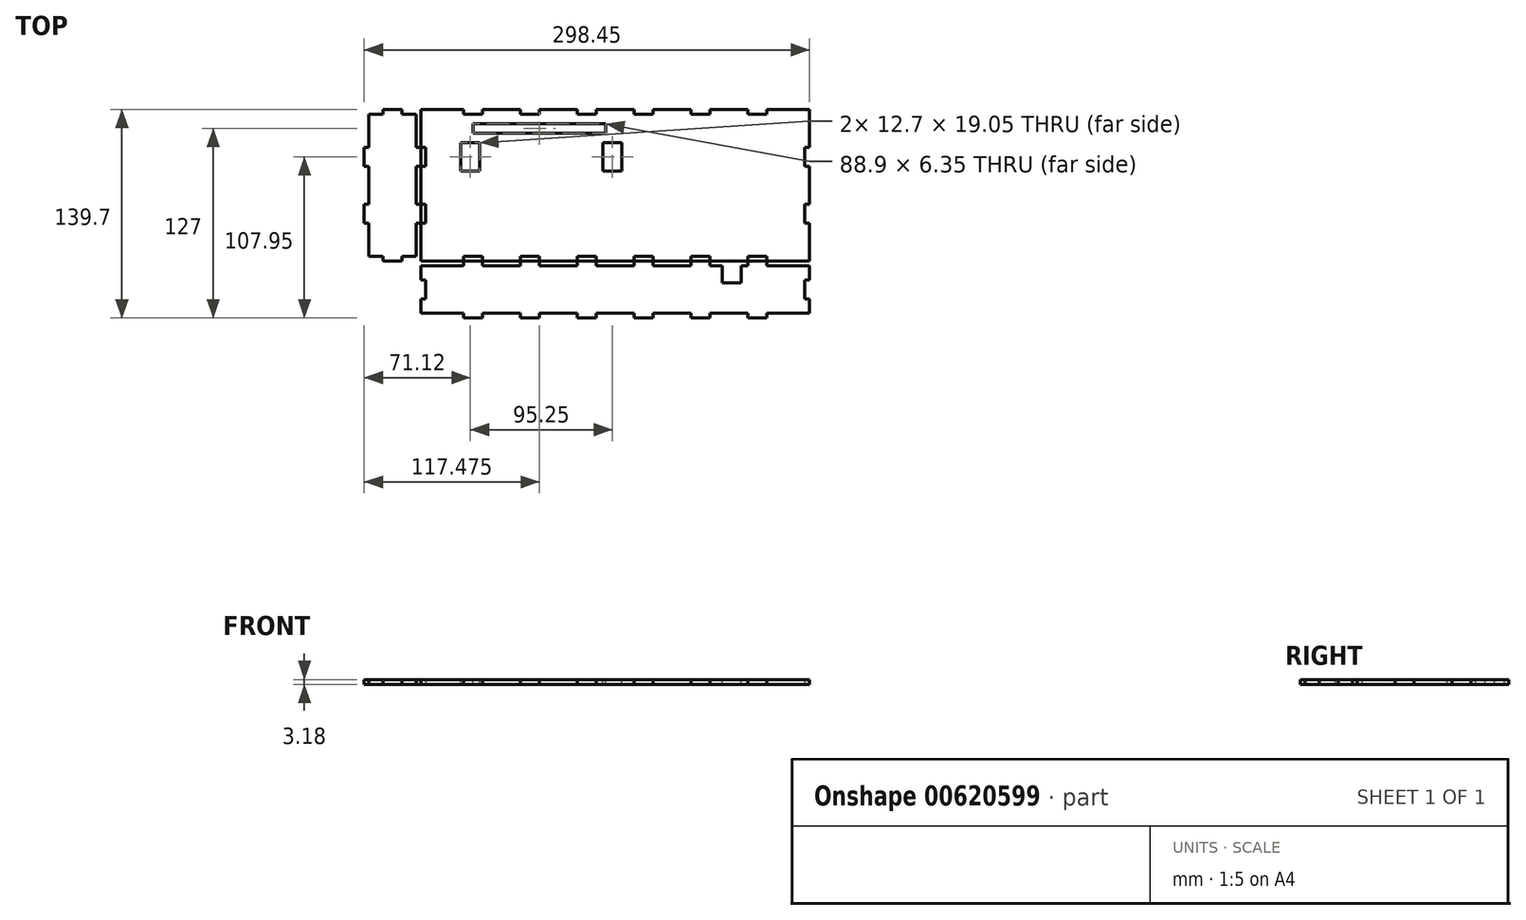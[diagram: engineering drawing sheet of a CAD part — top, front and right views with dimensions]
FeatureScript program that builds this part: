
annotation { "Feature Type Name" : "Feature", "Feature Type Description" : "" }
export const myFeature = defineFeature(function(context is Context, id is Id, definition is map)
    precondition{}
    {
        {
            var Q0;
            Q0=qCreatedBy(makeId("Top.planeOp"),FACE);
            var sketch = newSketch(context, id + "F0", { "sketchPlane" : qUnion([Q0])});
            skLineSegment(sketch, "E0.bottom", {"start": v(0, 0) * mm, "end": v(66.68, 0) * mm});
            skLineSegment(sketch, "E0.top", {"start": v(0, 101.6) * mm, "end": v(28.57, 101.6) * mm});
            skLineSegment(sketch, "E0.left", {"start": v(0, 0) * mm, "end": v(0, 25.4) * mm});
            skLineSegment(sketch, "E0.right", {"start": v(260.35, 0) * mm, "end": v(260.35, 25.4) * mm});
            skLineSegment(sketch, "E1.top", {"start": v(28.57, 98.42) * mm, "end": v(41.27, 98.42) * mm});
            skLineSegment(sketch, "E1.left", {"start": v(28.57, 101.6) * mm, "end": v(28.57, 98.42) * mm});
            skLineSegment(sketch, "E1.right", {"start": v(41.27, 101.6) * mm, "end": v(41.27, 98.42) * mm});
            skLineSegment(sketch, "E2.1.0.0", {"start": v(66.67, 98.42) * mm, "end": v(79.37, 98.42) * mm});
            skLineSegment(sketch, "E2.1.0.1", {"start": v(66.67, 101.6) * mm, "end": v(66.67, 98.42) * mm});
            skLineSegment(sketch, "E2.1.0.2", {"start": v(79.37, 101.6) * mm, "end": v(79.37, 98.42) * mm});
            skLineSegment(sketch, "E2.2.0.0", {"start": v(104.77, 98.42) * mm, "end": v(117.47, 98.42) * mm});
            skLineSegment(sketch, "E2.2.0.1", {"start": v(104.77, 101.6) * mm, "end": v(104.77, 98.42) * mm});
            skLineSegment(sketch, "E2.2.0.2", {"start": v(117.47, 101.6) * mm, "end": v(117.47, 98.42) * mm});
            skLineSegment(sketch, "E2.3.0.0", {"start": v(142.88, 98.42) * mm, "end": v(155.57, 98.42) * mm});
            skLineSegment(sketch, "E2.3.0.1", {"start": v(142.88, 101.6) * mm, "end": v(142.88, 98.42) * mm});
            skLineSegment(sketch, "E2.3.0.2", {"start": v(155.57, 101.6) * mm, "end": v(155.57, 98.42) * mm});
            skLineSegment(sketch, "E2.4.0.0", {"start": v(180.97, 98.42) * mm, "end": v(193.67, 98.42) * mm});
            skLineSegment(sketch, "E2.4.0.1", {"start": v(180.97, 101.6) * mm, "end": v(180.97, 98.42) * mm});
            skLineSegment(sketch, "E2.4.0.2", {"start": v(193.67, 101.6) * mm, "end": v(193.67, 98.42) * mm});
            skLineSegment(sketch, "E2.5.0.0", {"start": v(219.07, 98.42) * mm, "end": v(231.77, 98.42) * mm});
            skLineSegment(sketch, "E2.5.0.1", {"start": v(219.07, 101.6) * mm, "end": v(219.07, 98.42) * mm});
            skLineSegment(sketch, "E2.5.0.2", {"start": v(231.77, 101.6) * mm, "end": v(231.77, 98.42) * mm});
            skLineSegment(sketch, "E2.direction1", {"start": v(28.57, 98.42) * mm, "end": v(66.67, 98.42) * mm, "construction": true});
            skLineSegment(sketch, "E3.top", {"start": v(28.58, 3.17) * mm, "end": v(41.28, 3.17) * mm});
            skLineSegment(sketch, "E3.left", {"start": v(28.58, 0) * mm, "end": v(28.58, 3.17) * mm});
            skLineSegment(sketch, "E3.right", {"start": v(41.28, 0) * mm, "end": v(41.28, 3.17) * mm});
            skLineSegment(sketch, "E4.1.0.0", {"start": v(66.68, 3.17) * mm, "end": v(79.38, 3.17) * mm});
            skLineSegment(sketch, "E4.1.0.1", {"start": v(66.68, 0) * mm, "end": v(66.68, 3.17) * mm});
            skLineSegment(sketch, "E4.1.0.2", {"start": v(79.38, 0) * mm, "end": v(79.38, 3.17) * mm});
            skLineSegment(sketch, "E4.2.0.0", {"start": v(104.78, 3.17) * mm, "end": v(117.48, 3.17) * mm});
            skLineSegment(sketch, "E4.2.0.1", {"start": v(104.78, 0) * mm, "end": v(104.78, 3.17) * mm});
            skLineSegment(sketch, "E4.2.0.2", {"start": v(117.48, 0) * mm, "end": v(117.48, 3.17) * mm});
            skLineSegment(sketch, "E4.3.0.0", {"start": v(142.88, 3.17) * mm, "end": v(155.58, 3.17) * mm});
            skLineSegment(sketch, "E4.3.0.1", {"start": v(142.88, 0) * mm, "end": v(142.88, 3.17) * mm});
            skLineSegment(sketch, "E4.3.0.2", {"start": v(155.58, 0) * mm, "end": v(155.58, 3.17) * mm});
            skLineSegment(sketch, "E4.4.0.0", {"start": v(180.98, 3.17) * mm, "end": v(193.68, 3.17) * mm});
            skLineSegment(sketch, "E4.4.0.1", {"start": v(180.98, 0) * mm, "end": v(180.98, 3.17) * mm});
            skLineSegment(sketch, "E4.4.0.2", {"start": v(193.68, 0) * mm, "end": v(193.68, 3.17) * mm});
            skLineSegment(sketch, "E4.5.0.0", {"start": v(219.08, 3.17) * mm, "end": v(231.78, 3.17) * mm});
            skLineSegment(sketch, "E4.5.0.1", {"start": v(219.08, 0) * mm, "end": v(219.08, 3.17) * mm});
            skLineSegment(sketch, "E4.5.0.2", {"start": v(231.78, 0) * mm, "end": v(231.78, 3.17) * mm});
            skLineSegment(sketch, "E4.direction1", {"start": v(28.58, 3.17) * mm, "end": v(66.68, 3.17) * mm, "construction": true});
            skLineSegment(sketch, "E5.bottom", {"start": v(0, 76.2) * mm, "end": v(3.17, 76.2) * mm});
            skLineSegment(sketch, "E5.top", {"start": v(0, 63.5) * mm, "end": v(3.17, 63.5) * mm});
            skLineSegment(sketch, "E5.left", {"start": v(0, 76.2) * mm, "end": v(0, 63.5) * mm});
            skLineSegment(sketch, "E5.right", {"start": v(3.17, 76.2) * mm, "end": v(3.17, 63.5) * mm});
            skLineSegment(sketch, "E6.1.0.0", {"start": v(0, 38.1) * mm, "end": v(3.17, 38.1) * mm});
            skLineSegment(sketch, "E6.1.0.1", {"start": v(3.17, 38.1) * mm, "end": v(3.17, 25.4) * mm});
            skLineSegment(sketch, "E6.1.0.2", {"start": v(0, 25.4) * mm, "end": v(3.17, 25.4) * mm});
            skLineSegment(sketch, "E6.direction1", {"start": v(0, 63.5) * mm, "end": v(0, 38.1) * mm, "construction": true});
            skLineSegment(sketch, "E7.bottom", {"start": v(260.35, 76.2) * mm, "end": v(257.18, 76.2) * mm});
            skLineSegment(sketch, "E7.top", {"start": v(260.35, 63.5) * mm, "end": v(257.18, 63.5) * mm});
            skLineSegment(sketch, "E7.right", {"start": v(257.18, 76.2) * mm, "end": v(257.18, 63.5) * mm});
            skLineSegment(sketch, "E8.1.0.0", {"start": v(260.35, 38.1) * mm, "end": v(257.18, 38.1) * mm});
            skLineSegment(sketch, "E8.1.0.1", {"start": v(257.18, 38.1) * mm, "end": v(257.18, 25.4) * mm});
            skLineSegment(sketch, "E8.1.0.2", {"start": v(260.35, 25.4) * mm, "end": v(257.18, 25.4) * mm});
            skLineSegment(sketch, "E8.direction1", {"start": v(257.18, 76.2) * mm, "end": v(257.18, 38.1) * mm, "construction": true});
            skLineSegment(sketch, "E9.trimOffspring", {"start": v(41.27, 101.6) * mm, "end": v(66.67, 101.6) * mm});
            skLineSegment(sketch, "E10.trimOffspring", {"start": v(79.37, 101.6) * mm, "end": v(104.77, 101.6) * mm});
            skLineSegment(sketch, "E11.trimOffspring", {"start": v(117.47, 101.6) * mm, "end": v(142.88, 101.6) * mm});
            skLineSegment(sketch, "E12.trimOffspring", {"start": v(155.57, 101.6) * mm, "end": v(180.97, 101.6) * mm});
            skLineSegment(sketch, "E13.trimOffspring", {"start": v(193.67, 101.6) * mm, "end": v(219.07, 101.6) * mm});
            skLineSegment(sketch, "E14.trimOffspring", {"start": v(231.77, 101.6) * mm, "end": v(260.35, 101.6) * mm});
            skLineSegment(sketch, "E15.trimOffspring", {"start": v(0, 38.1) * mm, "end": v(0, 101.6) * mm});
            skLineSegment(sketch, "E16.trimOffspring", {"start": v(79.38, 0) * mm, "end": v(104.78, 0) * mm});
            skLineSegment(sketch, "E17.trimOffspring", {"start": v(117.48, 0) * mm, "end": v(142.88, 0) * mm});
            skLineSegment(sketch, "E18.trimOffspring", {"start": v(155.58, 0) * mm, "end": v(180.98, 0) * mm});
            skLineSegment(sketch, "E19.trimOffspring", {"start": v(193.68, 0) * mm, "end": v(219.08, 0) * mm});
            skLineSegment(sketch, "E20.trimOffspring", {"start": v(231.78, 0) * mm, "end": v(260.35, 0) * mm});
            skLineSegment(sketch, "E21.trimOffspring", {"start": v(260.35, 76.2) * mm, "end": v(260.35, 101.6) * mm});
            skLineSegment(sketch, "E22.trimOffspring", {"start": v(260.35, 38.1) * mm, "end": v(260.35, 63.5) * mm});
            skSolve(sketch);
        }
        {
            var Q0;
            {var subQ8=sQuery(id+"F0.wireOp",EDGE,"E0.top");Q0=makeQuery(id+"F0.imprint","IMPRINT",FACE,{"disambiguationData":[TD([[makeQuery(id+"F0.imprint","IMPRINT",EDGE,{"derivedFrom":subQ8}),-1.0]])]});}
            extrude(context, id + "F1", {"entities" : qUnion([Q0]), "depth" : 3.17 * mm, "offsetDistance" : 25.4 * mm});
        }
        {
            var Q0;
            Q0=qCreatedBy(makeId("Top.planeOp"),FACE);
            var sketch = newSketch(context, id + "F2", { "sketchPlane" : qUnion([Q0])});
            skLineSegment(sketch, "E23.bottom", {"start": v(0, 0) * mm, "end": v(41.28, 0) * mm});
            skLineSegment(sketch, "E23.top", {"start": v(28.58, -38.1) * mm, "end": v(41.28, -38.1) * mm});
            skLineSegment(sketch, "E23.left", {"start": v(0, -3.18) * mm, "end": v(0, -12.7) * mm});
            skLineSegment(sketch, "E23.right", {"start": v(260.35, -3.17) * mm, "end": v(260.35, -12.7) * mm});
            skLineSegment(sketch, "E24.top", {"start": v(0, -3.18) * mm, "end": v(28.58, -3.18) * mm});
            skLineSegment(sketch, "E24.right", {"start": v(28.58, 0) * mm, "end": v(28.58, -3.18) * mm});
            skLineSegment(sketch, "E25.top", {"start": v(41.28, -3.17) * mm, "end": v(66.68, -3.17) * mm});
            skLineSegment(sketch, "E25.left", {"start": v(41.28, 0) * mm, "end": v(41.28, -3.17) * mm});
            skLineSegment(sketch, "E25.right", {"start": v(66.68, 0) * mm, "end": v(66.68, -3.17) * mm});
            skLineSegment(sketch, "E26.1.0.0", {"start": v(79.38, 0) * mm, "end": v(79.38, -3.17) * mm});
            skLineSegment(sketch, "E26.1.0.1", {"start": v(79.38, -3.17) * mm, "end": v(104.78, -3.17) * mm});
            skLineSegment(sketch, "E26.1.0.2", {"start": v(104.78, 0) * mm, "end": v(104.78, -3.17) * mm});
            skLineSegment(sketch, "E26.2.0.0", {"start": v(117.47, 0) * mm, "end": v(117.47, -3.17) * mm});
            skLineSegment(sketch, "E26.2.0.1", {"start": v(117.47, -3.17) * mm, "end": v(142.88, -3.17) * mm});
            skLineSegment(sketch, "E26.2.0.2", {"start": v(142.88, 0) * mm, "end": v(142.88, -3.17) * mm});
            skLineSegment(sketch, "E26.3.0.0", {"start": v(155.57, 0) * mm, "end": v(155.57, -3.17) * mm});
            skLineSegment(sketch, "E26.3.0.1", {"start": v(155.57, -3.17) * mm, "end": v(180.97, -3.17) * mm});
            skLineSegment(sketch, "E26.3.0.2", {"start": v(180.97, 0) * mm, "end": v(180.97, -3.17) * mm});
            skLineSegment(sketch, "E26.4.0.0", {"start": v(193.67, 0) * mm, "end": v(193.67, -3.17) * mm});
            skLineSegment(sketch, "E26.4.0.1", {"start": v(193.67, -3.17) * mm, "end": v(219.07, -3.17) * mm});
            skLineSegment(sketch, "E26.4.0.2", {"start": v(219.07, 0) * mm, "end": v(219.07, -3.17) * mm});
            skLineSegment(sketch, "E26.direction1", {"start": v(41.28, -3.17) * mm, "end": v(79.38, -3.17) * mm, "construction": true});
            skLineSegment(sketch, "E27.top", {"start": v(231.78, -3.17) * mm, "end": v(260.35, -3.17) * mm});
            skLineSegment(sketch, "E27.left", {"start": v(231.78, 0) * mm, "end": v(231.78, -3.17) * mm});
            skLineSegment(sketch, "E28.bottom", {"start": v(0, -12.7) * mm, "end": v(3.18, -12.7) * mm});
            skLineSegment(sketch, "E28.top", {"start": v(0, -25.4) * mm, "end": v(3.18, -25.4) * mm});
            skLineSegment(sketch, "E28.right", {"start": v(3.18, -12.7) * mm, "end": v(3.18, -25.4) * mm});
            skLineSegment(sketch, "E29.top", {"start": v(0, -34.93) * mm, "end": v(28.58, -34.93) * mm});
            skLineSegment(sketch, "E29.right", {"start": v(28.58, -38.1) * mm, "end": v(28.58, -34.93) * mm});
            skLineSegment(sketch, "E30.top", {"start": v(41.28, -34.93) * mm, "end": v(66.68, -34.93) * mm});
            skLineSegment(sketch, "E30.left", {"start": v(41.28, -38.1) * mm, "end": v(41.28, -34.93) * mm});
            skLineSegment(sketch, "E30.right", {"start": v(66.68, -38.1) * mm, "end": v(66.68, -34.93) * mm});
            skLineSegment(sketch, "E31.1.0.0", {"start": v(79.38, -38.1) * mm, "end": v(79.38, -34.93) * mm});
            skLineSegment(sketch, "E31.1.0.1", {"start": v(79.38, -34.93) * mm, "end": v(104.78, -34.93) * mm});
            skLineSegment(sketch, "E31.1.0.2", {"start": v(104.78, -38.1) * mm, "end": v(104.78, -34.93) * mm});
            skLineSegment(sketch, "E31.2.0.0", {"start": v(117.47, -38.1) * mm, "end": v(117.47, -34.93) * mm});
            skLineSegment(sketch, "E31.2.0.1", {"start": v(117.47, -34.93) * mm, "end": v(142.88, -34.93) * mm});
            skLineSegment(sketch, "E31.2.0.2", {"start": v(142.88, -38.1) * mm, "end": v(142.88, -34.93) * mm});
            skLineSegment(sketch, "E31.3.0.0", {"start": v(155.57, -38.1) * mm, "end": v(155.57, -34.93) * mm});
            skLineSegment(sketch, "E31.3.0.1", {"start": v(155.57, -34.93) * mm, "end": v(180.97, -34.93) * mm});
            skLineSegment(sketch, "E31.3.0.2", {"start": v(180.97, -38.1) * mm, "end": v(180.97, -34.93) * mm});
            skLineSegment(sketch, "E31.4.0.0", {"start": v(193.67, -38.1) * mm, "end": v(193.67, -34.93) * mm});
            skLineSegment(sketch, "E31.4.0.1", {"start": v(193.67, -34.93) * mm, "end": v(219.07, -34.93) * mm});
            skLineSegment(sketch, "E31.4.0.2", {"start": v(219.07, -38.1) * mm, "end": v(219.07, -34.93) * mm});
            skLineSegment(sketch, "E31.direction1", {"start": v(66.68, -38.1) * mm, "end": v(79.38, -38.1) * mm, "construction": true});
            skLineSegment(sketch, "E32.top", {"start": v(231.78, -34.92) * mm, "end": v(260.35, -34.92) * mm});
            skLineSegment(sketch, "E32.left", {"start": v(231.78, -38.1) * mm, "end": v(231.78, -34.92) * mm});
            skLineSegment(sketch, "E33.bottom", {"start": v(260.35, -12.7) * mm, "end": v(257.18, -12.7) * mm});
            skLineSegment(sketch, "E33.top", {"start": v(260.35, -25.4) * mm, "end": v(257.18, -25.4) * mm});
            skLineSegment(sketch, "E33.right", {"start": v(257.18, -12.7) * mm, "end": v(257.18, -25.4) * mm});
            skLineSegment(sketch, "E34.trimOffspring", {"start": v(104.78, 0) * mm, "end": v(117.47, 0) * mm});
            skLineSegment(sketch, "E35.trimOffspring", {"start": v(66.68, 0) * mm, "end": v(79.38, 0) * mm});
            skLineSegment(sketch, "E36.trimOffspring", {"start": v(142.88, 0) * mm, "end": v(155.57, 0) * mm});
            skLineSegment(sketch, "E37.trimOffspring", {"start": v(180.97, 0) * mm, "end": v(193.67, 0) * mm});
            skLineSegment(sketch, "E38.trimOffspring", {"start": v(219.07, 0) * mm, "end": v(231.78, 0) * mm});
            skLineSegment(sketch, "E39.trimOffspring", {"start": v(260.35, -25.4) * mm, "end": v(260.35, -34.92) * mm});
            skLineSegment(sketch, "E40.trimOffspring", {"start": v(219.07, -38.1) * mm, "end": v(231.78, -38.1) * mm});
            skLineSegment(sketch, "E41.trimOffspring", {"start": v(180.97, -38.1) * mm, "end": v(193.67, -38.1) * mm});
            skLineSegment(sketch, "E42.trimOffspring", {"start": v(142.88, -38.1) * mm, "end": v(155.57, -38.1) * mm});
            skLineSegment(sketch, "E43.trimOffspring", {"start": v(104.78, -38.1) * mm, "end": v(117.47, -38.1) * mm});
            skLineSegment(sketch, "E44.trimOffspring", {"start": v(66.68, -38.1) * mm, "end": v(79.38, -38.1) * mm});
            skLineSegment(sketch, "E45.trimOffspring", {"start": v(0, -25.4) * mm, "end": v(0, -34.92) * mm});
            skSolve(sketch);
        }
        {
            var Q0;
            Q0=makeQuery(id+"F2.imprint","IMPRINT",FACE,{"disambiguationData":[TD([[makeQuery(id+"F2.imprint","IMPRINT",EDGE,{"derivedFrom":sQuery(id+"F2.wireOp",EDGE,"E23.top")}),1.0]])]});
            extrude(context, id + "F3", {"entities" : qUnion([Q0]), "depth" : 3.17 * mm, "offsetDistance" : 25.4 * mm});
        }
        {
            var Q0;
            Q0=qCreatedBy(makeId("Top.planeOp"),FACE);
            var sketch = newSketch(context, id + "F4", { "sketchPlane" : qUnion([Q0])});
            skLineSegment(sketch, "E46.left", {"start": v(0, 0) * mm, "end": v(0, 38.1) * mm});
            skLineSegment(sketch, "E46.right", {"start": v(-38.1, 25.4) * mm, "end": v(-38.1, 38.1) * mm});
            skLineSegment(sketch, "E47.top", {"start": v(0, 25.4) * mm, "end": v(-3.18, 25.4) * mm});
            skLineSegment(sketch, "E47.right", {"start": v(-3.17, 3.17) * mm, "end": v(-3.18, 25.4) * mm});
            skLineSegment(sketch, "E48.top", {"start": v(0, 76.2) * mm, "end": v(-3.18, 76.2) * mm});
            skLineSegment(sketch, "E48.right", {"start": v(-3.18, 98.42) * mm, "end": v(-3.18, 76.2) * mm});
            skLineSegment(sketch, "E49.bottom", {"start": v(0, 63.5) * mm, "end": v(-3.18, 63.5) * mm});
            skLineSegment(sketch, "E49.top", {"start": v(0, 38.1) * mm, "end": v(-3.18, 38.1) * mm});
            skLineSegment(sketch, "E49.right", {"start": v(-3.18, 63.5) * mm, "end": v(-3.18, 38.1) * mm});
            skLineSegment(sketch, "E50.MirrorCS", {"start": v(-34.93, 98.43) * mm, "end": v(-34.93, 76.2) * mm});
            skLineSegment(sketch, "E51.MirrorCS", {"start": v(-38.1, 76.2) * mm, "end": v(-34.93, 76.2) * mm});
            skLineSegment(sketch, "E52.MirrorCS", {"start": v(-38.1, 63.5) * mm, "end": v(-34.93, 63.5) * mm});
            skLineSegment(sketch, "E53.MirrorCS", {"start": v(-34.93, 63.5) * mm, "end": v(-34.93, 38.1) * mm});
            skLineSegment(sketch, "E54.MirrorCS", {"start": v(-38.1, 38.1) * mm, "end": v(-34.93, 38.1) * mm});
            skLineSegment(sketch, "E55.MirrorCS", {"start": v(-38.1, 25.4) * mm, "end": v(-34.93, 25.4) * mm});
            skLineSegment(sketch, "E56.MirrorCS", {"start": v(-34.93, 3.17) * mm, "end": v(-34.93, 25.4) * mm});
            skLineSegment(sketch, "E57.bottom", {"start": v(-25.4, 0) * mm, "end": v(-12.7, 0) * mm});
            skLineSegment(sketch, "E57.left", {"start": v(-25.4, 0) * mm, "end": v(-25.4, 3.17) * mm});
            skLineSegment(sketch, "E57.right", {"start": v(-12.7, 0) * mm, "end": v(-12.7, 3.18) * mm});
            skLineSegment(sketch, "E58.bottom", {"start": v(-25.4, 101.6) * mm, "end": v(-12.7, 101.6) * mm});
            skLineSegment(sketch, "E58.left", {"start": v(-25.4, 101.6) * mm, "end": v(-25.4, 98.43) * mm});
            skLineSegment(sketch, "E58.right", {"start": v(-12.7, 101.6) * mm, "end": v(-12.7, 98.43) * mm});
            skLineSegment(sketch, "E59", {"start": v(-25.4, 98.43) * mm, "end": v(-34.93, 98.43) * mm});
            skLineSegment(sketch, "E60", {"start": v(-34.93, 98.43) * mm, "end": v(-25.4, 98.43) * mm});
            skLineSegment(sketch, "E61", {"start": v(-25.4, 3.17) * mm, "end": v(-34.93, 3.17) * mm});
            skLineSegment(sketch, "E62", {"start": v(-34.93, 3.17) * mm, "end": v(-25.4, 3.17) * mm});
            skLineSegment(sketch, "E63.trimOffspring", {"start": v(-12.7, 0) * mm, "end": v(-25.4, 0) * mm});
            skLineSegment(sketch, "E64.trimOffspring", {"start": v(-12.7, 3.17) * mm, "end": v(-3.18, 3.17) * mm});
            skLineSegment(sketch, "E65.trimOffspring", {"start": v(-38.1, 63.5) * mm, "end": v(-38.1, 76.2) * mm});
            skLineSegment(sketch, "E66.trimOffspring", {"start": v(0, 63.5) * mm, "end": v(0, 76.2) * mm});
            skLineSegment(sketch, "E67.trimOffspring", {"start": v(-12.7, 101.6) * mm, "end": v(-25.4, 101.6) * mm});
            skLineSegment(sketch, "E68.trimOffspring", {"start": v(-12.7, 98.43) * mm, "end": v(-3.18, 98.42) * mm});
            skSolve(sketch);
        }
        {
            var Q0;
            Q0 = qSketchRegion(id + "F4", true);
            extrude(context, id + "F5", {"entities" : qUnion([Q0]), "depth" : 3.17 * mm, "offsetDistance" : 25.4 * mm});
        }
        {
            var Q0;
            Q0=makeQuery(id+"F1.opExtrude","CAP_FACE",FACE,{"disambiguationData":[OSD([sQuery(id+"F0.wireOp",EDGE,"E0.bottom"),sQuery(id+"F0.wireOp",EDGE,"E0.top"),sQuery(id+"F0.wireOp",EDGE,"E0.left"),sQuery(id+"F0.wireOp",EDGE,"E0.right"),sQuery(id+"F0.wireOp",EDGE,"E1.top"),sQuery(id+"F0.wireOp",EDGE,"E1.left"),sQuery(id+"F0.wireOp",EDGE,"E1.right"),sQuery(id+"F0.wireOp",EDGE,"E2.1.0.0"),sQuery(id+"F0.wireOp",EDGE,"E2.1.0.1"),sQuery(id+"F0.wireOp",EDGE,"E2.1.0.2"),sQuery(id+"F0.wireOp",EDGE,"E2.2.0.0"),sQuery(id+"F0.wireOp",EDGE,"E2.2.0.1"),sQuery(id+"F0.wireOp",EDGE,"E2.2.0.2"),sQuery(id+"F0.wireOp",EDGE,"E2.3.0.0"),sQuery(id+"F0.wireOp",EDGE,"E2.3.0.1"),sQuery(id+"F0.wireOp",EDGE,"E2.3.0.2"),sQuery(id+"F0.wireOp",EDGE,"E2.4.0.0"),sQuery(id+"F0.wireOp",EDGE,"E2.4.0.1"),sQuery(id+"F0.wireOp",EDGE,"E2.4.0.2"),sQuery(id+"F0.wireOp",EDGE,"E2.5.0.0"),sQuery(id+"F0.wireOp",EDGE,"E2.5.0.1"),sQuery(id+"F0.wireOp",EDGE,"E2.5.0.2"),sQuery(id+"F0.wireOp",EDGE,"E3.top"),sQuery(id+"F0.wireOp",EDGE,"E3.left"),sQuery(id+"F0.wireOp",EDGE,"E3.right"),sQuery(id+"F0.wireOp",EDGE,"E4.1.0.0"),sQuery(id+"F0.wireOp",EDGE,"E4.1.0.1"),sQuery(id+"F0.wireOp",EDGE,"E4.1.0.2"),sQuery(id+"F0.wireOp",EDGE,"E4.2.0.0"),sQuery(id+"F0.wireOp",EDGE,"E4.2.0.1"),sQuery(id+"F0.wireOp",EDGE,"E4.2.0.2"),sQuery(id+"F0.wireOp",EDGE,"E4.3.0.0"),sQuery(id+"F0.wireOp",EDGE,"E4.3.0.1"),sQuery(id+"F0.wireOp",EDGE,"E4.3.0.2"),sQuery(id+"F0.wireOp",EDGE,"E4.4.0.0"),sQuery(id+"F0.wireOp",EDGE,"E4.4.0.1"),sQuery(id+"F0.wireOp",EDGE,"E4.4.0.2"),sQuery(id+"F0.wireOp",EDGE,"E4.5.0.0"),sQuery(id+"F0.wireOp",EDGE,"E4.5.0.1"),sQuery(id+"F0.wireOp",EDGE,"E4.5.0.2"),sQuery(id+"F0.wireOp",EDGE,"E5.bottom"),sQuery(id+"F0.wireOp",EDGE,"E5.top"),sQuery(id+"F0.wireOp",EDGE,"E5.right"),sQuery(id+"F0.wireOp",EDGE,"E6.1.0.0"),sQuery(id+"F0.wireOp",EDGE,"E6.1.0.1"),sQuery(id+"F0.wireOp",EDGE,"E6.1.0.2"),sQuery(id+"F0.wireOp",EDGE,"E7.bottom"),sQuery(id+"F0.wireOp",EDGE,"E7.top"),sQuery(id+"F0.wireOp",EDGE,"E7.right"),sQuery(id+"F0.wireOp",EDGE,"E8.1.0.0"),sQuery(id+"F0.wireOp",EDGE,"E8.1.0.1"),sQuery(id+"F0.wireOp",EDGE,"E8.1.0.2"),sQuery(id+"F0.wireOp",EDGE,"E9.trimOffspring"),sQuery(id+"F0.wireOp",EDGE,"E10.trimOffspring"),sQuery(id+"F0.wireOp",EDGE,"E11.trimOffspring"),sQuery(id+"F0.wireOp",EDGE,"E12.trimOffspring"),sQuery(id+"F0.wireOp",EDGE,"E13.trimOffspring"),sQuery(id+"F0.wireOp",EDGE,"E14.trimOffspring"),sQuery(id+"F0.wireOp",EDGE,"E15.trimOffspring"),sQuery(id+"F0.wireOp",EDGE,"E16.trimOffspring"),sQuery(id+"F0.wireOp",EDGE,"E17.trimOffspring"),sQuery(id+"F0.wireOp",EDGE,"E18.trimOffspring"),sQuery(id+"F0.wireOp",EDGE,"E19.trimOffspring"),sQuery(id+"F0.wireOp",EDGE,"E20.trimOffspring"),sQuery(id+"F0.wireOp",EDGE,"E21.trimOffspring"),sQuery(id+"F0.wireOp",EDGE,"E22.trimOffspring")])],"isStart":false});
            var sketch = newSketch(context, id + "F6", { "sketchPlane" : qUnion([Q0])});
            skLineSegment(sketch, "E69.0.0", {"start": v(41.28, 3.17) * mm, "end": v(41.28, 0) * mm});
            skLineSegment(sketch, "E69.0.1", {"start": v(41.28, 0) * mm, "end": v(66.68, 0) * mm});
            skLineSegment(sketch, "E69.0.2", {"start": v(66.68, 0) * mm, "end": v(66.68, 3.17) * mm});
            skLineSegment(sketch, "E69.0.3", {"start": v(66.68, 3.17) * mm, "end": v(79.38, 3.17) * mm});
            skLineSegment(sketch, "E69.0.4", {"start": v(79.38, 3.17) * mm, "end": v(79.38, 0) * mm});
            skLineSegment(sketch, "E69.0.5", {"start": v(79.38, 0) * mm, "end": v(104.78, 0) * mm});
            skLineSegment(sketch, "E69.0.6", {"start": v(104.78, 0) * mm, "end": v(104.78, 3.17) * mm});
            skLineSegment(sketch, "E69.0.7", {"start": v(104.78, 3.17) * mm, "end": v(117.48, 3.17) * mm});
            skLineSegment(sketch, "E69.0.8", {"start": v(117.48, 3.17) * mm, "end": v(117.48, 0) * mm});
            skLineSegment(sketch, "E69.0.9", {"start": v(117.48, 0) * mm, "end": v(142.88, 0) * mm});
            skLineSegment(sketch, "E69.0.10", {"start": v(142.88, 0) * mm, "end": v(142.88, 3.17) * mm});
            skLineSegment(sketch, "E69.0.11", {"start": v(142.88, 3.17) * mm, "end": v(155.58, 3.17) * mm});
            skLineSegment(sketch, "E69.0.12", {"start": v(155.58, 3.17) * mm, "end": v(155.58, 0) * mm});
            skLineSegment(sketch, "E69.0.13", {"start": v(155.58, 0) * mm, "end": v(180.98, 0) * mm});
            skLineSegment(sketch, "E69.0.14", {"start": v(180.98, 0) * mm, "end": v(180.98, 3.17) * mm});
            skLineSegment(sketch, "E69.0.15", {"start": v(180.98, 3.17) * mm, "end": v(193.68, 3.17) * mm});
            skLineSegment(sketch, "E69.0.16", {"start": v(193.68, 3.17) * mm, "end": v(193.68, 0) * mm});
            skLineSegment(sketch, "E69.0.17", {"start": v(193.68, 0) * mm, "end": v(219.08, 0) * mm});
            skLineSegment(sketch, "E69.0.18", {"start": v(219.08, 0) * mm, "end": v(219.08, 3.17) * mm});
            skLineSegment(sketch, "E69.0.19", {"start": v(219.08, 3.17) * mm, "end": v(231.78, 3.17) * mm});
            skLineSegment(sketch, "E69.0.20", {"start": v(231.78, 3.17) * mm, "end": v(231.78, 0) * mm});
            skLineSegment(sketch, "E69.0.21", {"start": v(231.78, 0) * mm, "end": v(260.35, 0) * mm});
            skLineSegment(sketch, "E69.0.22", {"start": v(260.35, 0) * mm, "end": v(260.35, 25.4) * mm});
            skLineSegment(sketch, "E69.0.23", {"start": v(260.35, 25.4) * mm, "end": v(257.18, 25.4) * mm});
            skLineSegment(sketch, "E69.0.24", {"start": v(257.18, 25.4) * mm, "end": v(257.18, 38.1) * mm});
            skLineSegment(sketch, "E69.0.25", {"start": v(257.18, 38.1) * mm, "end": v(260.35, 38.1) * mm});
            skLineSegment(sketch, "E69.0.26", {"start": v(260.35, 38.1) * mm, "end": v(260.35, 63.5) * mm});
            skLineSegment(sketch, "E69.0.27", {"start": v(260.35, 63.5) * mm, "end": v(257.18, 63.5) * mm});
            skLineSegment(sketch, "E69.0.28", {"start": v(257.18, 63.5) * mm, "end": v(257.18, 76.2) * mm});
            skLineSegment(sketch, "E69.0.29", {"start": v(257.18, 76.2) * mm, "end": v(260.35, 76.2) * mm});
            skLineSegment(sketch, "E69.0.30", {"start": v(260.35, 76.2) * mm, "end": v(260.35, 101.6) * mm});
            skLineSegment(sketch, "E69.0.31", {"start": v(260.35, 101.6) * mm, "end": v(231.77, 101.6) * mm});
            skLineSegment(sketch, "E69.0.32", {"start": v(231.77, 101.6) * mm, "end": v(231.77, 98.42) * mm});
            skLineSegment(sketch, "E69.0.33", {"start": v(231.77, 98.42) * mm, "end": v(219.07, 98.42) * mm});
            skLineSegment(sketch, "E69.0.34", {"start": v(219.07, 98.42) * mm, "end": v(219.07, 101.6) * mm});
            skLineSegment(sketch, "E69.0.35", {"start": v(219.07, 101.6) * mm, "end": v(193.67, 101.6) * mm});
            skLineSegment(sketch, "E69.0.36", {"start": v(193.67, 101.6) * mm, "end": v(193.67, 98.42) * mm});
            skLineSegment(sketch, "E69.0.37", {"start": v(193.67, 98.42) * mm, "end": v(180.97, 98.42) * mm});
            skLineSegment(sketch, "E69.0.38", {"start": v(180.97, 98.42) * mm, "end": v(180.97, 101.6) * mm});
            skLineSegment(sketch, "E69.0.39", {"start": v(180.97, 101.6) * mm, "end": v(155.57, 101.6) * mm});
            skLineSegment(sketch, "E69.0.40", {"start": v(155.57, 101.6) * mm, "end": v(155.57, 98.42) * mm});
            skLineSegment(sketch, "E69.0.41", {"start": v(155.57, 98.42) * mm, "end": v(142.88, 98.42) * mm});
            skLineSegment(sketch, "E69.0.42", {"start": v(142.88, 98.42) * mm, "end": v(142.88, 101.6) * mm});
            skLineSegment(sketch, "E69.0.43", {"start": v(142.88, 101.6) * mm, "end": v(117.47, 101.6) * mm});
            skLineSegment(sketch, "E69.0.44", {"start": v(117.47, 101.6) * mm, "end": v(117.47, 98.42) * mm});
            skLineSegment(sketch, "E69.0.45", {"start": v(117.47, 98.42) * mm, "end": v(104.77, 98.42) * mm});
            skLineSegment(sketch, "E69.0.46", {"start": v(104.77, 98.42) * mm, "end": v(104.77, 101.6) * mm});
            skLineSegment(sketch, "E69.0.47", {"start": v(104.77, 101.6) * mm, "end": v(79.37, 101.6) * mm});
            skLineSegment(sketch, "E69.0.48", {"start": v(79.37, 101.6) * mm, "end": v(79.37, 98.42) * mm});
            skLineSegment(sketch, "E69.0.49", {"start": v(79.37, 98.42) * mm, "end": v(66.67, 98.42) * mm});
            skLineSegment(sketch, "E69.0.50", {"start": v(66.67, 98.42) * mm, "end": v(66.67, 101.6) * mm});
            skLineSegment(sketch, "E69.0.51", {"start": v(66.67, 101.6) * mm, "end": v(41.27, 101.6) * mm});
            skLineSegment(sketch, "E69.0.52", {"start": v(41.27, 101.6) * mm, "end": v(41.27, 98.42) * mm});
            skLineSegment(sketch, "E69.0.53", {"start": v(41.27, 98.42) * mm, "end": v(28.57, 98.42) * mm});
            skLineSegment(sketch, "E69.0.54", {"start": v(28.57, 98.42) * mm, "end": v(28.57, 101.6) * mm});
            skLineSegment(sketch, "E69.0.55", {"start": v(28.57, 101.6) * mm, "end": v(0, 101.6) * mm});
            skLineSegment(sketch, "E69.0.56", {"start": v(0, 101.6) * mm, "end": v(0, 76.2) * mm});
            skLineSegment(sketch, "E69.0.57", {"start": v(0, 76.2) * mm, "end": v(3.17, 76.2) * mm});
            skLineSegment(sketch, "E69.0.58", {"start": v(3.17, 76.2) * mm, "end": v(3.17, 63.5) * mm});
            skLineSegment(sketch, "E69.0.59", {"start": v(3.17, 63.5) * mm, "end": v(0, 63.5) * mm});
            skLineSegment(sketch, "E69.0.60", {"start": v(0, 63.5) * mm, "end": v(0, 38.1) * mm});
            skLineSegment(sketch, "E69.0.61", {"start": v(0, 38.1) * mm, "end": v(3.17, 38.1) * mm});
            skLineSegment(sketch, "E69.0.62", {"start": v(3.17, 38.1) * mm, "end": v(3.17, 25.4) * mm});
            skLineSegment(sketch, "E69.0.63", {"start": v(3.17, 25.4) * mm, "end": v(0, 25.4) * mm});
            skLineSegment(sketch, "E69.0.64", {"start": v(0, 25.4) * mm, "end": v(0, 0) * mm});
            skLineSegment(sketch, "E69.0.65", {"start": v(0, 0) * mm, "end": v(28.58, 0) * mm});
            skLineSegment(sketch, "E69.0.66", {"start": v(28.58, 0) * mm, "end": v(28.58, 3.17) * mm});
            skLineSegment(sketch, "E69.0.67", {"start": v(28.58, 3.17) * mm, "end": v(41.28, 3.17) * mm});
            skLineSegment(sketch, "E70.bottom", {"start": v(34.92, 92.07) * mm, "end": v(123.82, 92.07) * mm});
            skLineSegment(sketch, "E70.top", {"start": v(34.92, 85.72) * mm, "end": v(123.82, 85.72) * mm});
            skLineSegment(sketch, "E70.left", {"start": v(34.92, 92.07) * mm, "end": v(34.92, 85.72) * mm});
            skLineSegment(sketch, "E70.right", {"start": v(123.82, 92.07) * mm, "end": v(123.82, 85.72) * mm});
            skLineSegment(sketch, "E71.bottom", {"start": v(26.67, 79.37) * mm, "end": v(39.37, 79.37) * mm});
            skLineSegment(sketch, "E71.top", {"start": v(26.67, 60.32) * mm, "end": v(39.37, 60.32) * mm});
            skLineSegment(sketch, "E71.left", {"start": v(26.67, 79.37) * mm, "end": v(26.67, 60.32) * mm});
            skLineSegment(sketch, "E71.right", {"start": v(39.37, 79.37) * mm, "end": v(39.37, 60.32) * mm});
            skLineSegment(sketch, "E72.bottom", {"start": v(121.92, 79.37) * mm, "end": v(134.62, 79.37) * mm});
            skLineSegment(sketch, "E72.top", {"start": v(121.92, 60.32) * mm, "end": v(134.62, 60.32) * mm});
            skLineSegment(sketch, "E72.left", {"start": v(121.92, 79.37) * mm, "end": v(121.92, 60.32) * mm});
            skLineSegment(sketch, "E72.right", {"start": v(134.62, 79.37) * mm, "end": v(134.62, 60.32) * mm});
            skLineSegment(sketch, "E73.bottom", {"start": v(214.63, -3.17) * mm, "end": v(201.93, -3.17) * mm});
            skLineSegment(sketch, "E73.top", {"start": v(214.63, -14.6) * mm, "end": v(201.93, -14.6) * mm});
            skLineSegment(sketch, "E73.left", {"start": v(214.63, -3.18) * mm, "end": v(214.63, -14.6) * mm});
            skLineSegment(sketch, "E73.right", {"start": v(201.93, -3.18) * mm, "end": v(201.93, -14.6) * mm});
            skPoint(sketch, "E74", {"position": v(208.28, -8.89) * mm});
            skPoint(sketch, "E74.positionSnap0", {"position": v(214.63, -8.89) * mm});
            skPoint(sketch, "E74.positionSnap1", {"position": v(208.28, -3.17) * mm});
            skSolve(sketch);
        }
        {
            var Q0;
            Q0=makeQuery(id+"F6.imprint","IMPRINT",FACE,{"disambiguationData":[TD([[makeQuery(id+"F6.imprint","IMPRINT",EDGE,{"derivedFrom":sQuery(id+"F6.wireOp",EDGE,"E71.bottom")}),-1.0]])]});
            var Q1;
            Q1=makeQuery(id+"F6.imprint","IMPRINT",FACE,{"disambiguationData":[TD([[makeQuery(id+"F6.imprint","IMPRINT",EDGE,{"derivedFrom":sQuery(id+"F6.wireOp",EDGE,"E70.bottom")}),-1.0]])]});
            var Q2;
            Q2=makeQuery(id+"F6.imprint","IMPRINT",FACE,{"disambiguationData":[TD([[makeQuery(id+"F6.imprint","IMPRINT",EDGE,{"derivedFrom":sQuery(id+"F6.wireOp",EDGE,"E72.bottom")}),-1.0]])]});
            var Q3;
            Q3=makeQuery(id+"F6.imprint","IMPRINT",FACE,{"disambiguationData":[TD([[makeQuery(id+"F6.imprint","IMPRINT",EDGE,{"derivedFrom":sQuery(id+"F6.wireOp",EDGE,"E73.bottom")}),1.0]])]});
            extrude(context, id + "F7", {"entities" : qUnion([Q0, Q1, Q2, Q3]), "operationType" : NewBodyOperationType.REMOVE, "endBound" : BoundingType.THROUGH_ALL, "oppositeDirection" : true, "depth" : 25.4 * mm, "offsetDistance" : 25.4 * mm});
        }
    });
